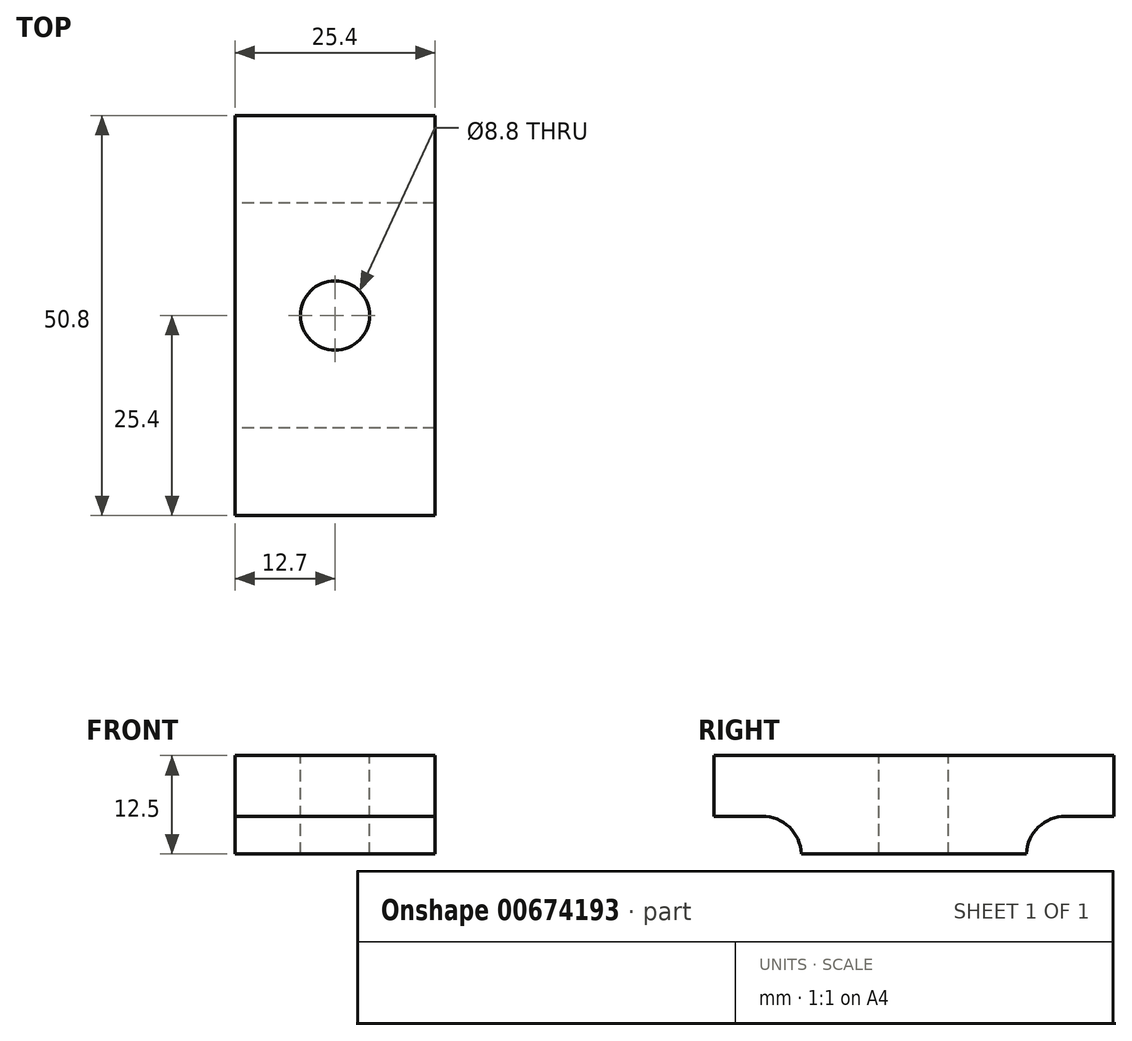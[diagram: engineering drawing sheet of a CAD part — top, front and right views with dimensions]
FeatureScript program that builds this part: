
annotation { "Feature Type Name" : "Feature", "Feature Type Description" : "" }
export const myFeature = defineFeature(function(context is Context, id is Id, definition is map)
    precondition{}
    {
        {
            var Q0;
            Q0=qCreatedBy(makeId("Right.planeOp"),FACE);
            var sketch = newSketch(context, id + "F0", { "sketchPlane" : qUnion([Q0])});
            skLineSegment(sketch, "E0.top", {"start": v(-25.4, 6.35) * mm, "end": v(25.4, 6.35) * mm});
            skLineSegment(sketch, "E0.left", {"start": v(-25.4, -1.35) * mm, "end": v(-25.4, 6.35) * mm});
            skLineSegment(sketch, "E0.right", {"start": v(25.4, -1.35) * mm, "end": v(25.4, 6.35) * mm});
            skPoint(sketch, "E0.middle", {"position": v(0, 0) * mm});
            skArc(sketch, "E1", {"start": v(19.29, -1.35) * mm, "mid": v(15.82, -2.74) * mm, "end": v(14.3, -6.15) * mm});
            skArc(sketch, "E2", {"start": v(-14.3, -6.15) * mm, "mid": v(-15.82, -2.74) * mm, "end": v(-19.29, -1.35) * mm});
            skLineSegment(sketch, "E3", {"start": v(25.4, -1.35) * mm, "end": v(19.29, -1.35) * mm});
            skPoint(sketch, "E4.trimOffspring.end.orphan", {"position": v(25.4, -6.35) * mm});
            skLineSegment(sketch, "E5.trimOffspring", {"start": v(-14.3, -6.15) * mm, "end": v(14.3, -6.15) * mm});
            skLineSegment(sketch, "E6.trimOffspring", {"start": v(-19.29, -1.35) * mm, "end": v(-25.4, -1.35) * mm});
            skSolve(sketch);
        }
        {
            var Q0;
            Q0=makeQuery(id+"F0.imprint","IMPRINT",FACE,{"disambiguationData":[TD([[makeQuery(id+"F0.imprint","IMPRINT",EDGE,{"derivedFrom":sQuery(id+"F0.wireOp",EDGE,"E0.top")}),-1.0]])]});
            extrude(context, id + "F1", {"entities" : qUnion([Q0]), "endBound" : BoundingType.SYMMETRIC, "depth" : 25.4 * mm, "offsetDistance" : 25 * mm});
        }
        {
            var Q0;
            Q0=makeQuery(id+"F1.opExtrude","SWEPT_FACE",FACE,{"disambiguationData":[OSD([sQuery(id+"F0.wireOp",EDGE,"E0.top")])]});
            var sketch = newSketch(context, id + "F2", { "sketchPlane" : qUnion([Q0])});
            skLineSegment(sketch, "E7", {"start": v(-12.7, 25.4) * mm, "end": v(12.7, -25.4) * mm, "construction": true});
            skCircle(sketch, "E8", {"center": v(0, 0) * mm, "radius": 4.4 * mm});
            skSolve(sketch);
        }
        {
            var Q0;
            Q0=makeQuery(id+"F2.imprint","IMPRINT",FACE,{"disambiguationData":[TD([[makeQuery(id+"F2.imprint","IMPRINT",EDGE,{"derivedFrom":sQuery(id+"F2.wireOp",EDGE,"E8")}),1.0]])]});
            extrude(context, id + "F3", {"entities" : qUnion([Q0]), "operationType" : NewBodyOperationType.REMOVE, "oppositeDirection" : true, "depth" : 25 * mm, "offsetDistance" : 25 * mm});
        }
    });
